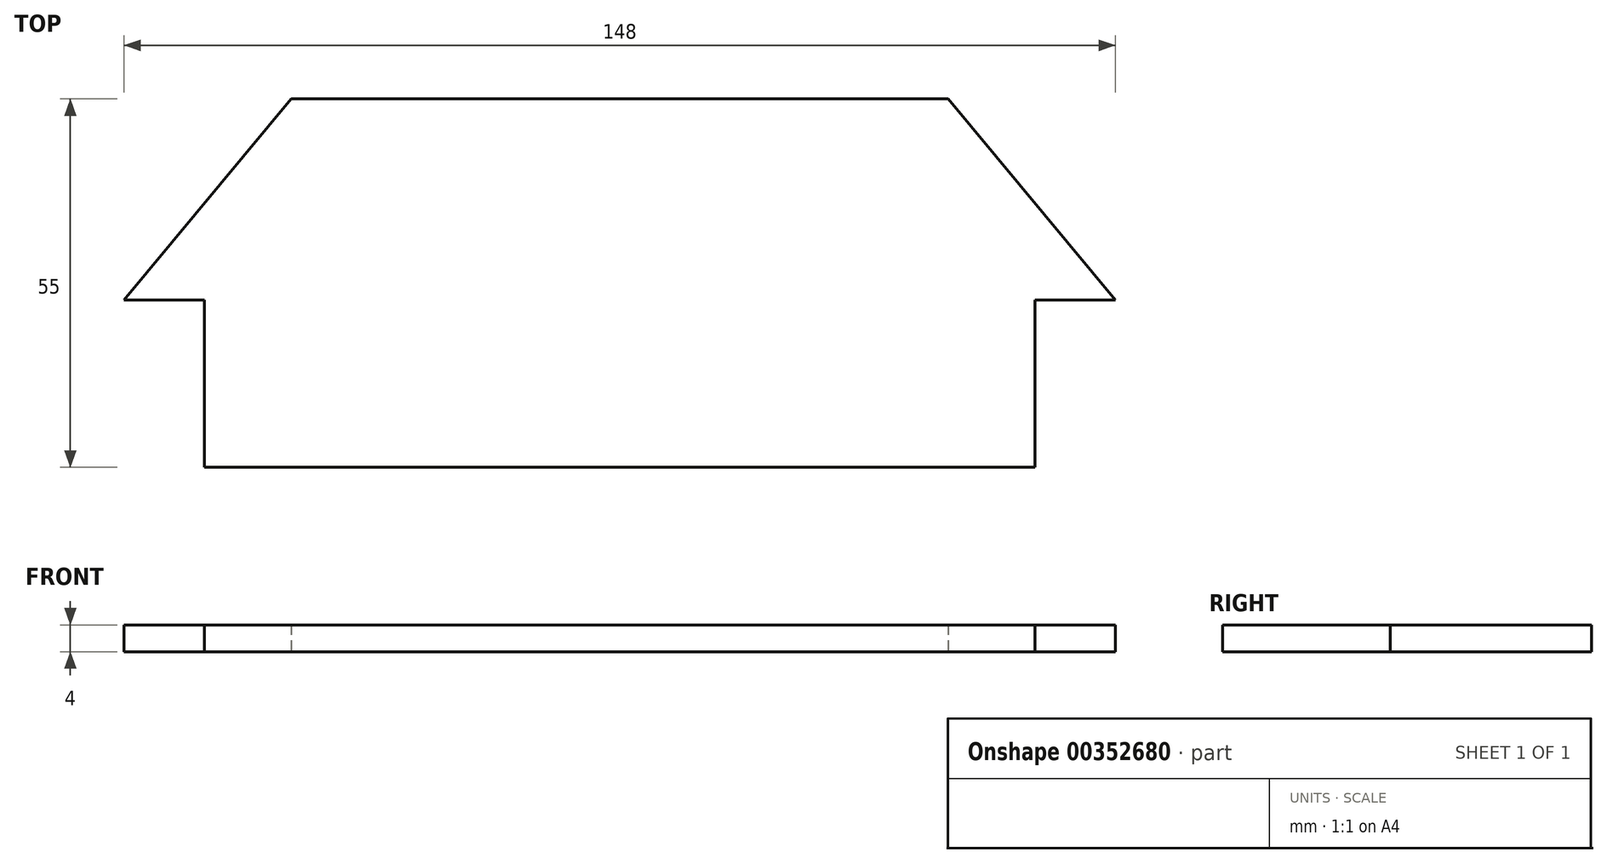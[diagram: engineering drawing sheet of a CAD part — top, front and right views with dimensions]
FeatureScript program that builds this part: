
annotation { "Feature Type Name" : "Feature", "Feature Type Description" : "" }
export const myFeature = defineFeature(function(context is Context, id is Id, definition is map)
    precondition{}
    {
        {
            var Q0;
            Q0=qCreatedBy(makeId("Top.planeOp"),FACE);
            var sketch = newSketch(context, id + "F0", { "sketchPlane" : qUnion([Q0])});
            skLineSegment(sketch, "E0.bottom", {"start": v(-49, 27.5) * mm, "end": v(49, 27.5) * mm});
            skLineSegment(sketch, "E0.top", {"start": v(-62, -27.5) * mm, "end": v(62, -27.5) * mm});
            skPoint(sketch, "E0.middle", {"position": v(0, 0) * mm});
            skLineSegment(sketch, "E1", {"start": v(-62, -27.5) * mm, "end": v(-62, -2.5) * mm});
            skLineSegment(sketch, "E2", {"start": v(-62, -2.5) * mm, "end": v(-74, -2.5) * mm});
            skLineSegment(sketch, "E3", {"start": v(-74, -2.5) * mm, "end": v(-49, 27.5) * mm});
            skLineSegment(sketch, "E4.MirrorCS", {"start": v(74, -2.5) * mm, "end": v(49, 27.5) * mm});
            skLineSegment(sketch, "E5.MirrorCS", {"start": v(62, -2.5) * mm, "end": v(74, -2.5) * mm});
            skLineSegment(sketch, "E6.MirrorCS", {"start": v(62, -27.5) * mm, "end": v(62, -2.5) * mm});
            skSolve(sketch);
        }
        {
            var Q0;
            Q0 = qSketchRegion(id + "F0", true);
            extrude(context, id + "F1", {"entities" : qUnion([Q0]), "depth" : 4 * mm});
        }
    });
